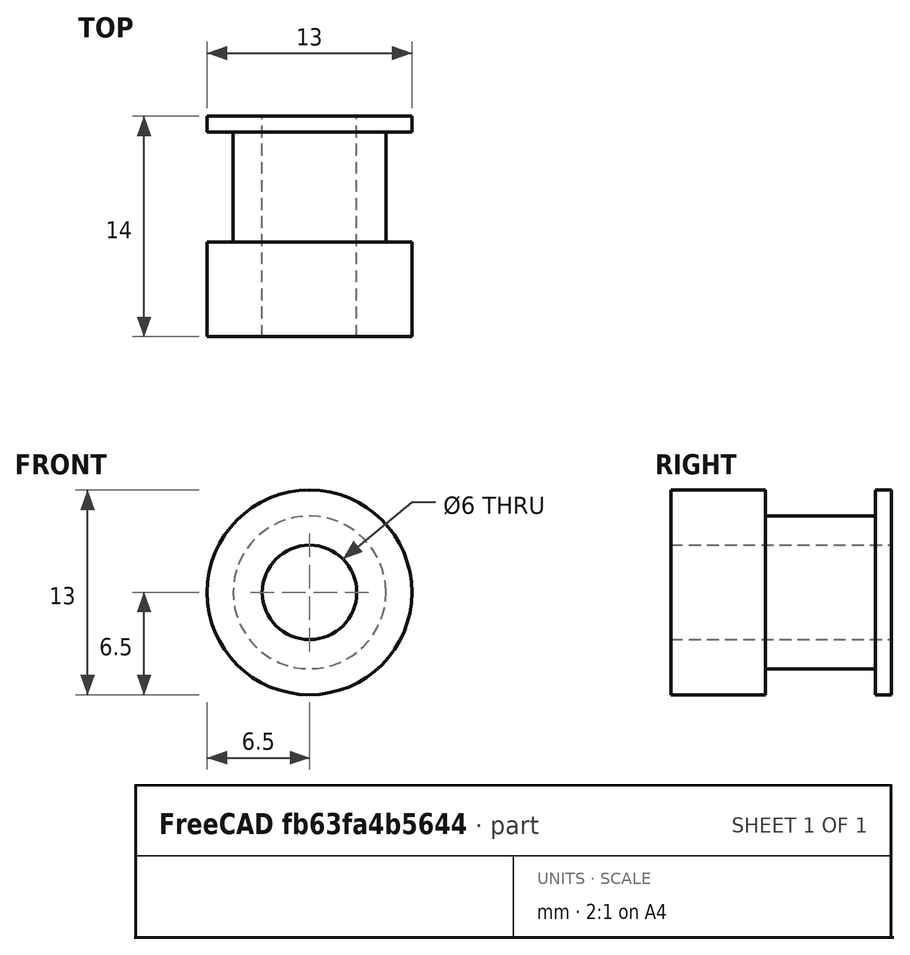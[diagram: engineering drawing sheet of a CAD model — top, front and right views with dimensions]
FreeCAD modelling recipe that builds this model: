
FCSTD DOCUMENT  (FreeCAD 0.16RUnknown)
Label: timing_pulley_gt2_16T
License: All rights reserved
LicenseURL: http://en.wikipedia.org/wiki/All_rights_reserved
objects: Sketcher::SketchObject×1, PartDesign::Revolution×1
note: 3 computed .brp shape members not serialized (recipe doc carries the construction recipe); baked Part::Feature solids carry a one-line shape summary decoded from their .brp

FEATURE [Sketcher::SketchObject] Sketch
  sketch-geometry (9):
    g0: LineSegment StartX=3 StartY=0 StartZ=0 EndX=3 EndY=14 EndZ=0
    g1: LineSegment StartX=3 StartY=14 StartZ=0 EndX=6.5 EndY=14 EndZ=0
    g2: LineSegment StartX=6.5 StartY=6 StartZ=0 EndX=6.5 EndY=0 EndZ=0
    g3: LineSegment StartX=6.5 StartY=0 StartZ=0 EndX=3 EndY=0 EndZ=0
    g4: LineSegment StartX=6.5 StartY=6 StartZ=0 EndX=4.85 EndY=6 EndZ=0
    g5: LineSegment StartX=4.85 StartY=6 StartZ=0 EndX=4.85 EndY=13 EndZ=0
    g6: LineSegment StartX=4.85 StartY=13 StartZ=0 EndX=6.5 EndY=13 EndZ=0
    g7: LineSegment StartX=6.5 StartY=13 StartZ=0 EndX=6.5 EndY=14 EndZ=0
    g8: LineSegment [constr] StartX=6.5 StartY=6 StartZ=0 EndX=6.5 EndY=13 EndZ=0
  constraints (26):
    c: Vertical(g0)
    c: Coincident(g0,g1)
    c: Horizontal(g1)
    c: Vertical(g2)
    c: Coincident(g2,g3)
    c: Coincident(g3,g0)
    c: Horizontal(g3)
    c: DistanceY(g0,g0) = 14
    c: PointOnObject(g0,g-1)
    c: DistanceX(g-1,g2) = 6.5
    c: DistanceX(g-1,g0) = 3
    c: Horizontal(g4)
    c: Coincident(g4,g5)
    c: Vertical(g5)
    c: Coincident(g5,g6)
    c: Horizontal(g6)
    c: Coincident(g6,g7)
    c: Coincident(g7,g1)
    c: Vertical(g7)
    c: Coincident(g8,g6)
    c: Vertical(g8)
    c: Coincident(g4,g8)
    c: Coincident(g4,g2)
    c: DistanceX(g-1,g5) = 4.85
    c: DistanceY(g8,g8) = 7
    c: DistanceY(g2,g2) = 6
FEATURE [PartDesign::Revolution] Revolution
  Angle = 360
  Axis = (0,1,0)
  Base = (0,0,0)
  ReferenceAxis = -> Sketch [V_Axis]
  Reversed = true
  Sketch = -> Sketch
